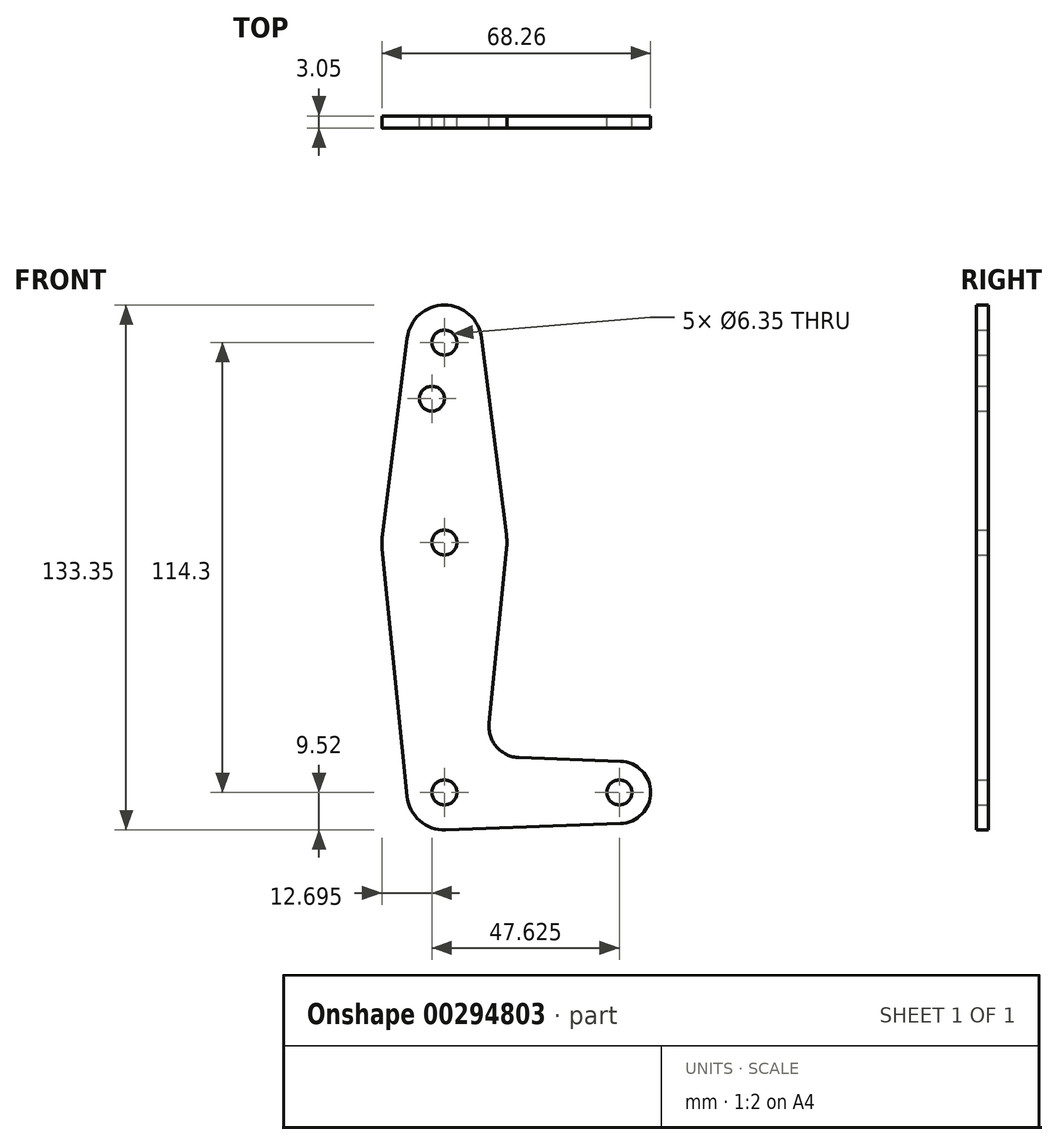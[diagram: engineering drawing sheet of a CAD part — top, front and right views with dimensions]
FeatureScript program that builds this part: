
annotation { "Feature Type Name" : "Feature", "Feature Type Description" : "" }
export const myFeature = defineFeature(function(context is Context, id is Id, definition is map)
    precondition{}
    {
        {
            var Q0;
            Q0=qCreatedBy(makeId("Front.planeOp"),FACE);
            var sketch = newSketch(context, id + "F0", { "sketchPlane" : qUnion([Q0])});
            skCircle(sketch, "E0", {"center": v(0, 63.5) * mm, "radius": 15.88 * mm});
            skCircle(sketch, "E1", {"center": v(0, 114.3) * mm, "radius": 9.53 * mm});
            skCircle(sketch, "E2", {"center": v(0, 0) * mm, "radius": 9.53 * mm});
            skLineSegment(sketch, "E3", {"start": v(0, 0) * mm, "end": v(44.45, 0) * mm, "construction": true});
            skLineSegment(sketch, "E4", {"start": v(0, 0) * mm, "end": v(0, 114.3) * mm, "construction": true});
            skCircle(sketch, "E5", {"center": v(44.45, 0) * mm, "radius": 7.94 * mm});
            skLineSegment(sketch, "E6", {"start": v(-9.48, -0.95) * mm, "end": v(-15.8, 61.91) * mm});
            skLineSegment(sketch, "E7", {"start": v(-15.75, 65.48) * mm, "end": v(-9.45, 115.5) * mm});
            skLineSegment(sketch, "E8", {"start": v(44.73, -7.93) * mm, "end": v(0.34, -9.52) * mm});
            skLineSegment(sketch, "E9", {"start": v(9.45, 115.5) * mm, "end": v(15.75, 65.48) * mm});
            skLineSegment(sketch, "E10", {"start": v(15.8, 61.91) * mm, "end": v(11.34, 17.6) * mm});
            skLineSegment(sketch, "E11", {"start": v(18.97, 8.85) * mm, "end": v(44.73, 7.93) * mm});
            skCircle(sketch, "E12", {"center": v(0, 114.3) * mm, "radius": 3.18 * mm});
            skCircle(sketch, "E13", {"center": v(0, 63.5) * mm, "radius": 3.18 * mm});
            skCircle(sketch, "E14", {"center": v(0, 0) * mm, "radius": 3.18 * mm});
            skCircle(sketch, "E15", {"center": v(44.45, 0) * mm, "radius": 3.18 * mm});
            skCircle(sketch, "E16", {"center": v(-3.18, 100.03) * mm, "radius": 3.18 * mm});
            skArc(sketch, "E17.filletArc", {"start": v(11.34, 17.6) * mm, "mid": v(13.26, 11.57) * mm, "end": v(18.97, 8.85) * mm});
            skSolve(sketch);
        }
        {
            var Q0;
            Q0 = qSketchRegion(id + "F0", true);
            extrude(context, id + "F1", {"entities" : qUnion([Q0]), "depth" : 3.05 * mm});
        }
    });
